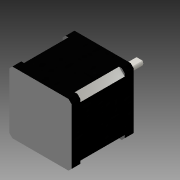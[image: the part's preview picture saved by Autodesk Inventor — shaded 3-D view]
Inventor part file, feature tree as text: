
AUTODESK INVENTOR PART (.ipt)
format: ipt  version: 2016 (Build 200138000, 138)  size: 192,512 bytes
history: native  units: mm
features: sketch x6, extrude x5, thread x4, mirror x2, fillet x1, hole x1, plane x1, chamfer x1
ambient origin geometry x8: Origin, YZ Plane, XZ Plane, XY Plane, X Axis, Y Axis, Z Axis, Center Point
bodies: 实体1 (feature_tree)
feature tree (21):
  extrude  "拉伸1"  Depth=42.0mm TaperAngle=0.0deg
  extrude  "拉伸2"  Depth=25.0mm
  fillet  "圆角1"  Radius=1.0mm
  hole  "孔1"  [1 undecoded]
  thread  "螺纹1"  [1 undecoded]
  thread  "螺纹2"  [1 undecoded]
  thread  "螺纹3"  [1 undecoded]
  thread  "螺纹4"  [1 undecoded]
  extrude  "拉伸3"  Depth=10.0mm TaperAngle=0.0deg
  extrude  "拉伸4"  Depth=25.0mm TaperAngle=0.0deg
  plane  "工作平面1"
  extrude  "拉伸5"  Depth=1.5mm
  mirror  "镜像1"
  mirror  "镜像2"
  chamfer  "倒角1"  Distance=15.0mm
  sketch  "草图1"  dims[d0=42.0mm d1=42.0mm d2=0.0mm]
  sketch  "草图2"  dims[d3=30.0mm d4=25.0mm d5=1.0mm d6=0.0mm]
  sketch  "草图3"  dims[d7=0.3mm d8=3.0mm d9=18.0mm d10=18.0mm]
  sketch  "草图4"  dims[d11=3.0mm d12=0.599mm d13=4.0mm d14=2.0mm d15=90.0deg d16=10.0mm d17=20.594885mm d18=10.0mm d19=0.0mm d20=10.0mm d21=0.0mm]
  sketch  "草图5"  dims[d22=10.0mm d23=0.0mm d24=10.0mm d25=0.0mm]
  sketch  "草图6"  dims[d26=5.0mm d27=25.0mm d28=0.0mm d29=1.5mm d30=15.0mm d31=0.0mm d32=-21.0mm d34=45.0deg d35=30.0mm d36=0.0mm d37=2.0mm d38=2.0mm d39=45.0deg]
note: 5 required parameter values undecoded (feature->parameter linkage not recoverable at this tier; creation-order binding heuristic only, values carry confidence <= 0.55)
